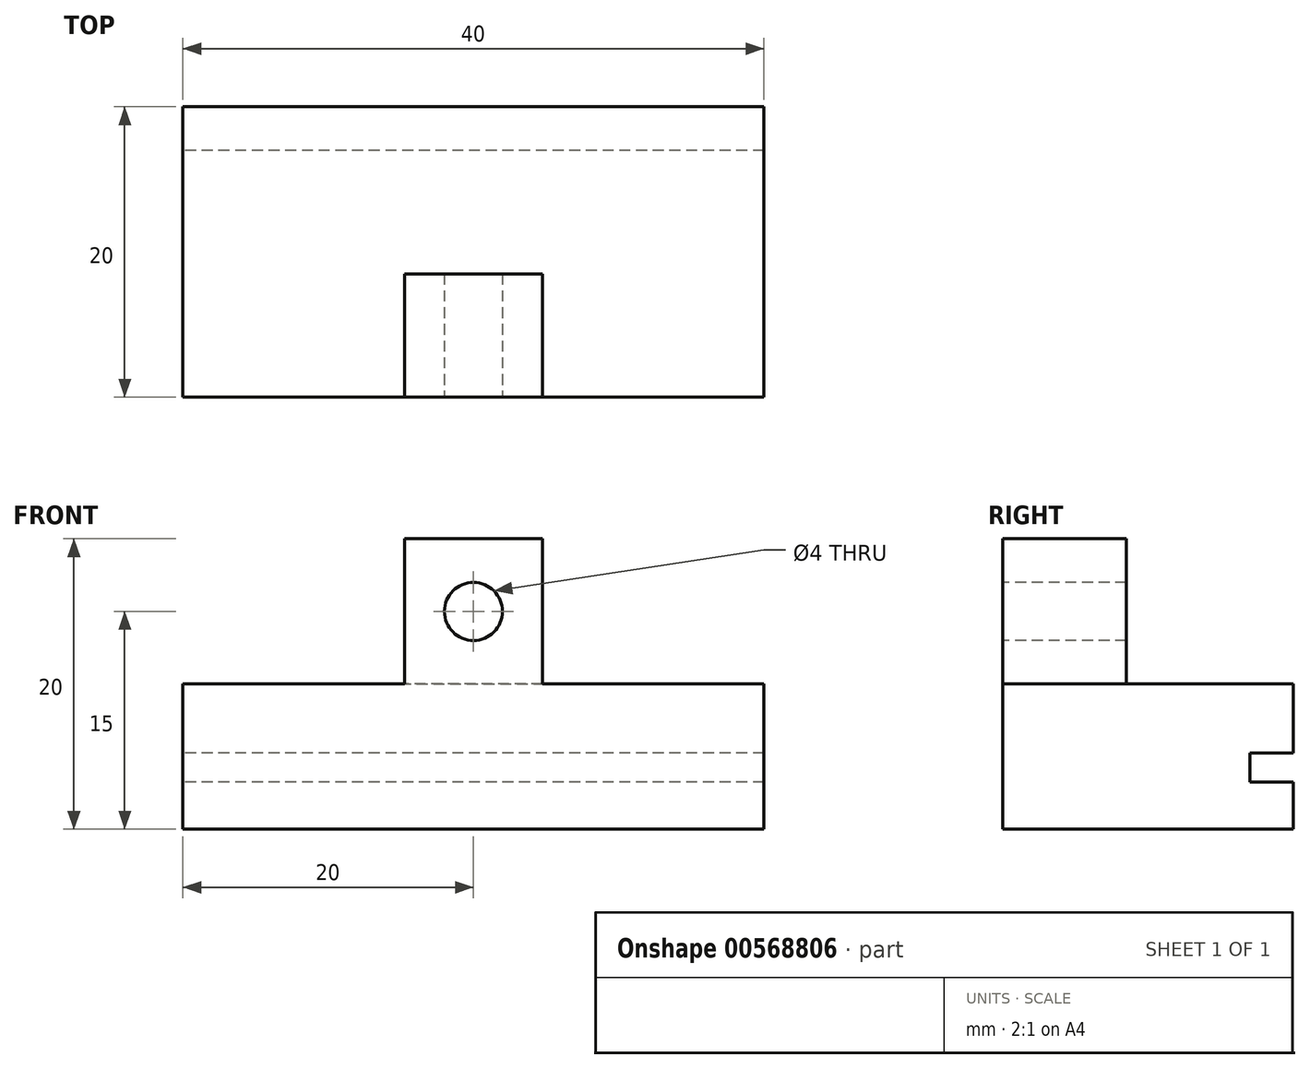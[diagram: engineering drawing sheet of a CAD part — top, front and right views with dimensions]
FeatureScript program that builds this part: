
annotation { "Feature Type Name" : "Feature", "Feature Type Description" : "" }
export const myFeature = defineFeature(function(context is Context, id is Id, definition is map)
    precondition{}
    {
        {
            var Q0;
            Q0=qCreatedBy(makeId("Top.planeOp"),FACE);
            var sketch = newSketch(context, id + "F0", { "sketchPlane" : qUnion([Q0])});
            skLineSegment(sketch, "E0.bottom", {"start": v(-20, 10) * mm, "end": v(20, 10) * mm});
            skLineSegment(sketch, "E0.top", {"start": v(-20, -10) * mm, "end": v(20, -10) * mm});
            skLineSegment(sketch, "E0.left", {"start": v(-20, 10) * mm, "end": v(-20, -10) * mm});
            skLineSegment(sketch, "E0.right", {"start": v(20, 10) * mm, "end": v(20, -10) * mm});
            skSolve(sketch);
        }
        {
            var Q0;
            Q0=makeQuery(id+"F0.imprint","IMPRINT",FACE,{"disambiguationData":[TD([[makeQuery(id+"F0.imprint","IMPRINT",EDGE,{"derivedFrom":sQuery(id+"F0.wireOp",EDGE,"E0.bottom")}),-1.0]])]});
            extrude(context, id + "F1", {"entities" : qUnion([Q0]), "depth" : 10 * mm, "offsetDistance" : 25 * mm});
        }
        {
            var Q0;
            Q0=makeQuery(id+"F1.opExtrude","CAP_FACE",FACE,{"disambiguationData":[OSD([sQuery(id+"F0.wireOp",EDGE,"E0.bottom"),sQuery(id+"F0.wireOp",EDGE,"E0.top"),sQuery(id+"F0.wireOp",EDGE,"E0.left"),sQuery(id+"F0.wireOp",EDGE,"E0.right")])],"isStart":false});
            var sketch = newSketch(context, id + "F2", { "sketchPlane" : qUnion([Q0])});
            skLineSegment(sketch, "E1.bottom", {"start": v(4.75, -10) * mm, "end": v(-4.75, -10) * mm});
            skLineSegment(sketch, "E1.top", {"start": v(4.75, -1.5) * mm, "end": v(-4.75, -1.5) * mm});
            skLineSegment(sketch, "E1.left", {"start": v(4.75, -10) * mm, "end": v(4.75, -1.5) * mm});
            skLineSegment(sketch, "E1.right", {"start": v(-4.75, -10) * mm, "end": v(-4.75, -1.5) * mm});
            skPoint(sketch, "E1.middle", {"position": v(0, -5.75) * mm});
            skSolve(sketch);
        }
        {
            var Q0;
            Q0=makeQuery(id+"F2.imprint","IMPRINT",FACE,{"disambiguationData":[TD([[makeQuery(id+"F2.imprint","IMPRINT",EDGE,{"derivedFrom":sQuery(id+"F2.wireOp",EDGE,"E1.bottom")}),1.0]])]});
            extrude(context, id + "F3", {"entities" : qUnion([Q0]), "operationType" : NewBodyOperationType.ADD, "depth" : 10 * mm, "offsetDistance" : 25 * mm});
        }
        {
            var Q0;
            Q0=makeQuery(id+"F3.boolean.opBoolean","MERGE",FACE,{"derivedFrom":[makeQuery(id+"F1.opExtrude","SWEPT_FACE",FACE,{"disambiguationData":[OSD([sQuery(id+"F0.wireOp",EDGE,"E0.top")])]}),makeQuery(id+"F3.opExtrude","SWEPT_FACE",FACE,{"disambiguationData":[OSD([sQuery(id+"F2.wireOp",EDGE,"E1.bottom")])]})]});
            var sketch = newSketch(context, id + "F4", { "sketchPlane" : qUnion([Q0])});
            skCircle(sketch, "E2", {"center": v(0, 15) * mm, "radius": 2 * mm});
            skSolve(sketch);
        }
        {
            var Q0;
            Q0=makeQuery(id+"F4.imprint","IMPRINT",FACE,{"disambiguationData":[TD([[makeQuery(id+"F4.imprint","IMPRINT",EDGE,{"derivedFrom":sQuery(id+"F4.wireOp",EDGE,"E2")}),1.0]])]});
            extrude(context, id + "F5", {"entities" : qUnion([Q0]), "operationType" : NewBodyOperationType.REMOVE, "oppositeDirection" : true, "depth" : 10 * mm, "offsetDistance" : 25 * mm});
        }
        {
            var Q0;
            Q0=makeQuery(id+"F1.opExtrude","SWEPT_FACE",FACE,{"disambiguationData":[OSD([sQuery(id+"F0.wireOp",EDGE,"E0.bottom")])]});
            var sketch = newSketch(context, id + "F6", { "sketchPlane" : qUnion([Q0])});
            skLineSegment(sketch, "E3.bottom", {"start": v(-20, 5.25) * mm, "end": v(20, 5.25) * mm});
            skLineSegment(sketch, "E3.top", {"start": v(-20, 3.25) * mm, "end": v(20, 3.25) * mm});
            skLineSegment(sketch, "E3.left", {"start": v(-20, 5.25) * mm, "end": v(-20, 3.25) * mm});
            skLineSegment(sketch, "E3.right", {"start": v(20, 5.25) * mm, "end": v(20, 3.25) * mm});
            skSolve(sketch);
        }
        {
            var Q0;
            Q0=makeQuery(id+"F6.imprint","IMPRINT",FACE,{"disambiguationData":[TD([[makeQuery(id+"F6.imprint","IMPRINT",EDGE,{"derivedFrom":sQuery(id+"F6.wireOp",EDGE,"E3.bottom")}),-1.0]])]});
            extrude(context, id + "F7", {"entities" : qUnion([Q0]), "operationType" : NewBodyOperationType.REMOVE, "oppositeDirection" : true, "depth" : 3 * mm, "offsetDistance" : 25 * mm});
        }
    });
